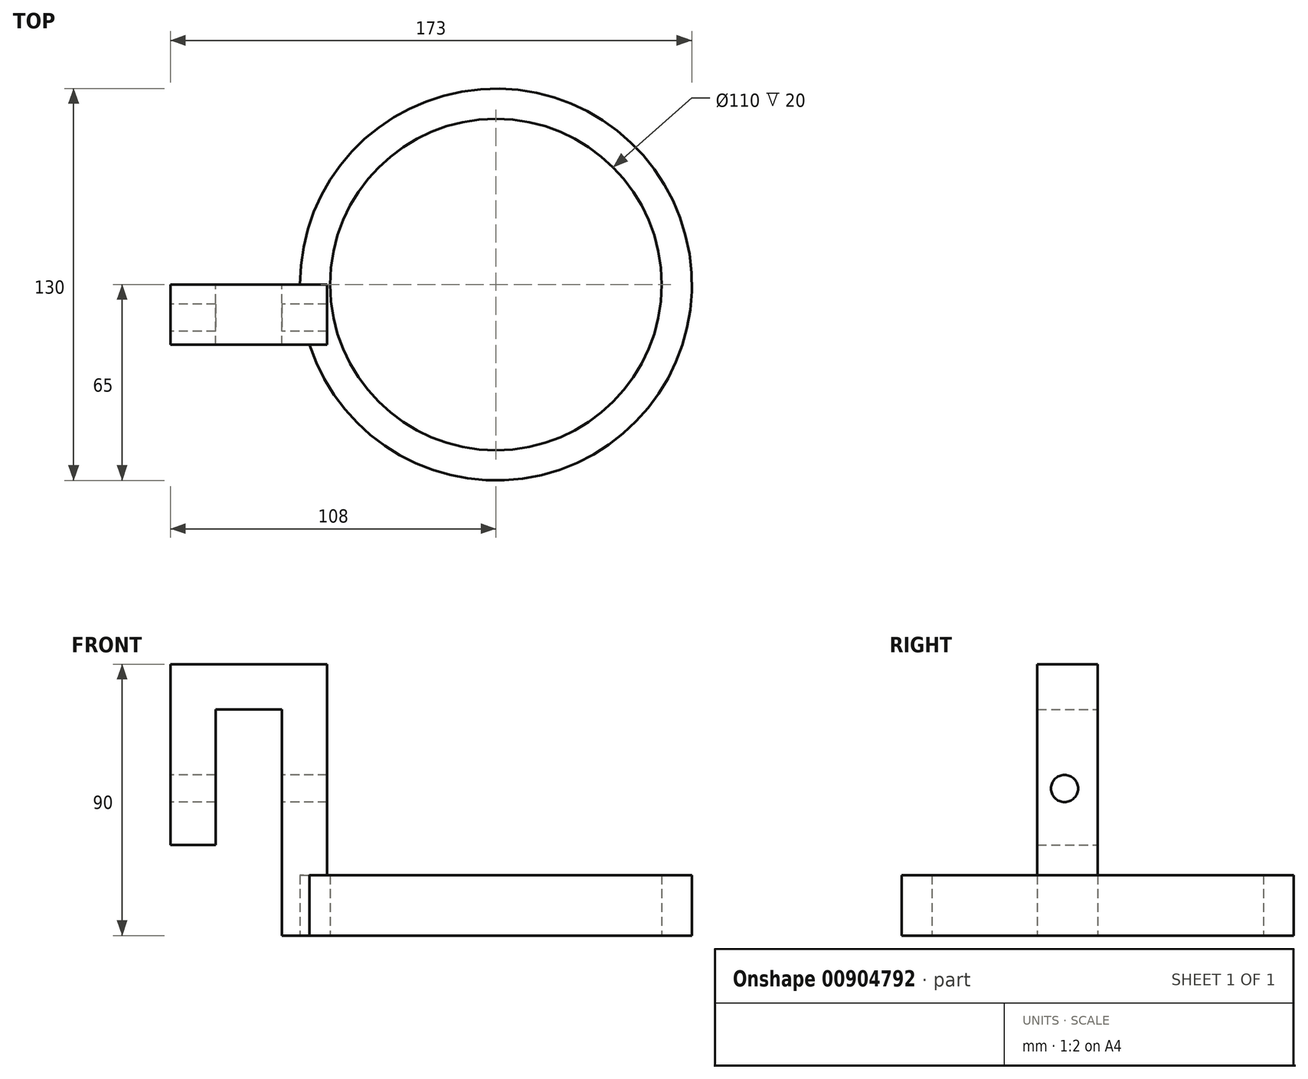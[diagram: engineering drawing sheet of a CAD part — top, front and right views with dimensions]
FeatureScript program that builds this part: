
annotation { "Feature Type Name" : "Feature", "Feature Type Description" : "" }
export const myFeature = defineFeature(function(context is Context, id is Id, definition is map)
    precondition{}
    {
        {
            var Q0;
            Q0=qCreatedBy(makeId("Top.planeOp"),FACE);
            var sketch = newSketch(context, id + "F0", { "sketchPlane" : qUnion([Q0])});
            skCircle(sketch, "E0", {"center": v(0, 0) * mm, "radius": 65 * mm});
            skCircle(sketch, "E1", {"center": v(0, 0) * mm, "radius": 55 * mm});
            skSolve(sketch);
        }
        {
            var Q0;
            Q0=makeQuery(id+"F0.imprint","IMPRINT",FACE,{"disambiguationData":[TD([[makeQuery(id+"F0.imprint","IMPRINT",EDGE,{"derivedFrom":sQuery(id+"F0.wireOp",EDGE,"E0")}),1.0]])]});
            extrude(context, id + "F1", {"entities" : qUnion([Q0]), "depth" : 20 * mm, "offsetDistance" : 25 * mm});
        }
        {
            var Q0;
            Q0=qCreatedBy(makeId("Front.planeOp"),FACE);
            var sketch = newSketch(context, id + "F2", { "sketchPlane" : qUnion([Q0])});
            skLineSegment(sketch, "E2.bottom", {"start": v(-56, 0) * mm, "end": v(-71, 0) * mm});
            skLineSegment(sketch, "E2.top", {"start": v(-56, 90) * mm, "end": v(-71, 90) * mm});
            skLineSegment(sketch, "E2.left", {"start": v(-56, 0) * mm, "end": v(-56, 90) * mm});
            skLineSegment(sketch, "E2.right", {"start": v(-71, 0) * mm, "end": v(-71, 75) * mm});
            skLineSegment(sketch, "E3", {"start": v(-71, 90) * mm, "end": v(-108, 90) * mm});
            skLineSegment(sketch, "E4", {"start": v(-108, 90) * mm, "end": v(-108, 30) * mm});
            skLineSegment(sketch, "E5", {"start": v(-108, 30) * mm, "end": v(-93, 30) * mm});
            skLineSegment(sketch, "E6", {"start": v(-93, 30) * mm, "end": v(-93, 75) * mm});
            skLineSegment(sketch, "E7", {"start": v(-93, 75) * mm, "end": v(-71, 75) * mm});
            skSolve(sketch);
        }
        {
            var Q0;
            Q0=makeQuery(id+"F2.imprint","IMPRINT",FACE,{"disambiguationData":[TD([[makeQuery(id+"F2.imprint","IMPRINT",EDGE,{"derivedFrom":sQuery(id+"F2.wireOp",EDGE,"E2.bottom")}),-1.0]])]});
            extrude(context, id + "F3", {"entities" : qUnion([Q0]), "operationType" : NewBodyOperationType.ADD, "depth" : 20 * mm, "offsetDistance" : 25 * mm});
        }
        {
            var Q0;
            Q0=makeQuery(id+"F3.opExtrude","SWEPT_FACE",FACE,{"disambiguationData":[OSD([sQuery(id+"F2.wireOp",EDGE,"E4")])]});
            var sketch = newSketch(context, id + "F4", { "sketchPlane" : qUnion([Q0])});
            skCircle(sketch, "E8", {"center": v(11, 48.8) * mm, "radius": 4.5 * mm});
            skSolve(sketch);
        }
        {
            var Q0;
            Q0=makeQuery(id+"F4.imprint","IMPRINT",FACE,{"disambiguationData":[TD([[makeQuery(id+"F4.imprint","IMPRINT",EDGE,{"derivedFrom":sQuery(id+"F4.wireOp",EDGE,"E8")}),1.0]])]});
            extrude(context, id + "F5", {"entities" : qUnion([Q0]), "operationType" : NewBodyOperationType.REMOVE, "endBound" : BoundingType.THROUGH_ALL, "oppositeDirection" : true, "depth" : 25 * mm, "offsetDistance" : 25 * mm});
        }
    });
